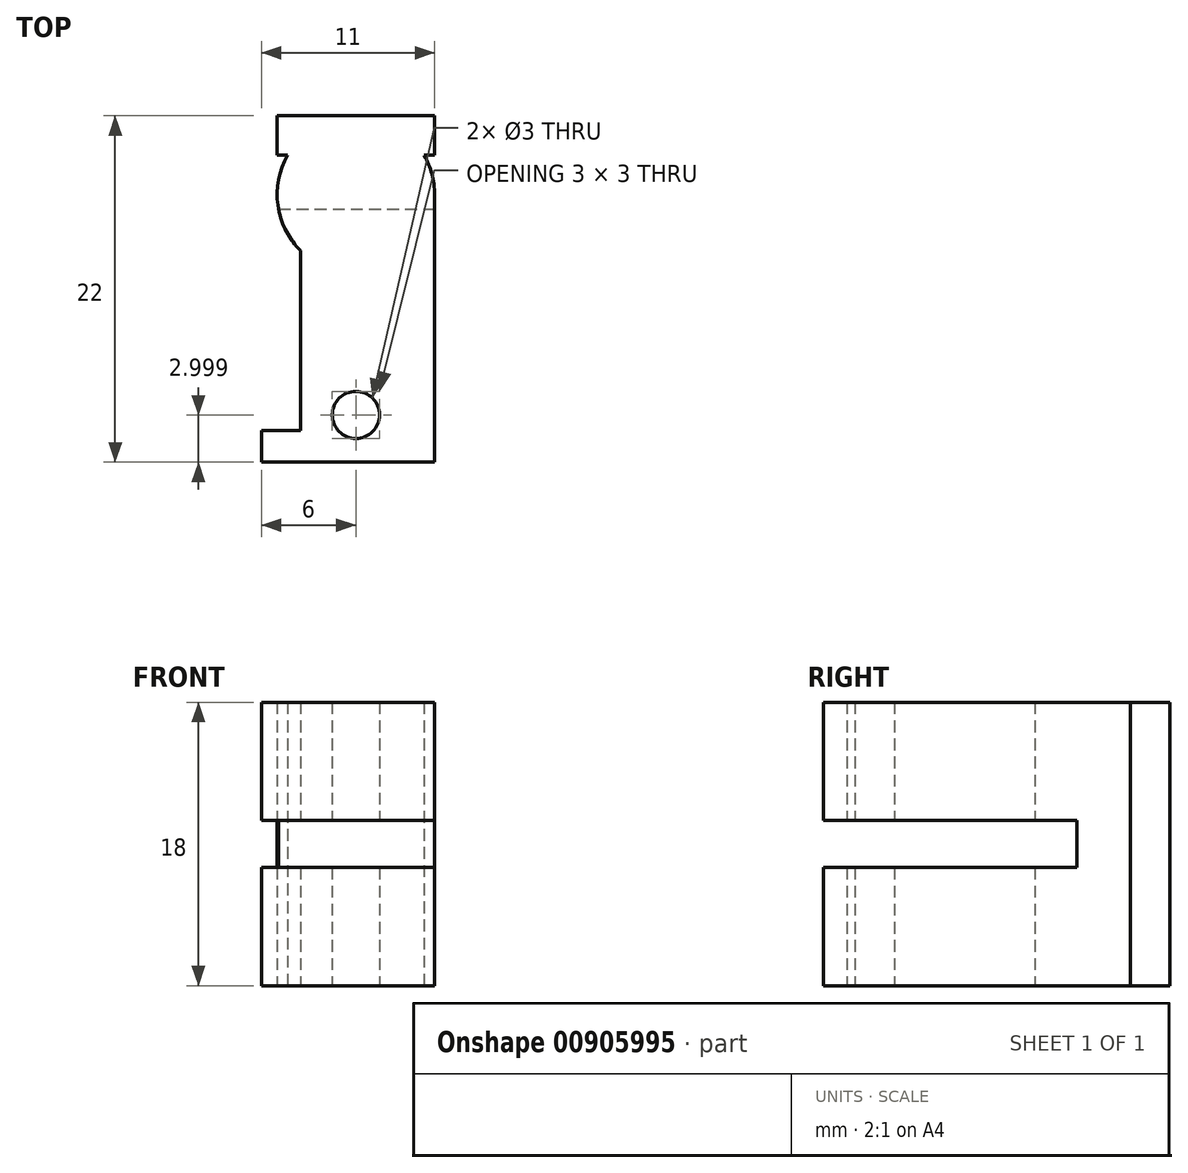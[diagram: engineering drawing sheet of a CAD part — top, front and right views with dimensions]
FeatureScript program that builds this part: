
annotation { "Feature Type Name" : "Feature", "Feature Type Description" : "" }
export const myFeature = defineFeature(function(context is Context, id is Id, definition is map)
    precondition{}
    {
        {
            var Q0;
            Q0=qCreatedBy(makeId("Top.planeOp"),FACE);
            var sketch = newSketch(context, id + "F0", { "sketchPlane" : qUnion([Q0])});
            skLineSegment(sketch, "E0.bottom", {"start": v(5, -1.25) * mm, "end": v(4.33, -1.25) * mm});
            skLineSegment(sketch, "E0.top", {"start": v(5, 1.25) * mm, "end": v(-5, 1.25) * mm});
            skLineSegment(sketch, "E0.left", {"start": v(5, -1.25) * mm, "end": v(5, 1.25) * mm});
            skLineSegment(sketch, "E0.right", {"start": v(-5, -1.25) * mm, "end": v(-5, 1.25) * mm});
            skPoint(sketch, "E0.middle", {"position": v(0, 0) * mm});
            skArc(sketch, "E1", {"start": v(5, -3.75) * mm, "mid": v(4.83, -2.46) * mm, "end": v(4.33, -1.25) * mm});
            skLineSegment(sketch, "E2.left", {"start": v(-3.5, -7.32) * mm, "end": v(-3.5, -18.75) * mm});
            skLineSegment(sketch, "E2.right", {"start": v(5, -3.75) * mm, "end": v(5, -18.75) * mm});
            skLineSegment(sketch, "E3.bottom", {"start": v(-3.5, -18.75) * mm, "end": v(-6, -18.75) * mm});
            skLineSegment(sketch, "E3.top", {"start": v(5, -20.75) * mm, "end": v(-6, -20.75) * mm});
            skLineSegment(sketch, "E3.left", {"start": v(5, -18.75) * mm, "end": v(5, -20.75) * mm});
            skLineSegment(sketch, "E3.right", {"start": v(-6, -18.75) * mm, "end": v(-6, -20.75) * mm});
            skCircle(sketch, "E4", {"center": v(0, -17.75) * mm, "radius": 1.5 * mm});
            skArc(sketch, "E5.trimOffspring", {"start": v(-4.33, -1.25) * mm, "mid": v(-4.95, -4.43) * mm, "end": v(-3.5, -7.32) * mm});
            skLineSegment(sketch, "E6.trimOffspring", {"start": v(-4.33, -1.25) * mm, "end": v(-5, -1.25) * mm});
            skSolve(sketch);
        }
        {
            var Q0;
            Q0=makeQuery(id+"F0.imprint","IMPRINT",FACE,{"disambiguationData":[TD([[makeQuery(id+"F0.imprint","IMPRINT",EDGE,{"derivedFrom":sQuery(id+"F0.wireOp",EDGE,"E0.bottom")}),-1.0]])]});
            extrude(context, id + "F1", {"entities" : qUnion([Q0]), "depth" : 18 * mm, "offsetDistance" : 25.4 * mm});
        }
        {
            var Q0;
            Q0=makeQuery(id+"F1.opExtrude","SWEPT_FACE",FACE,{"disambiguationData":[OSD([sQuery(id+"F0.wireOp",EDGE,"E2.right"),sQuery(id+"F0.wireOp",EDGE,"E3.left")])]});
            var sketch = newSketch(context, id + "F2", { "sketchPlane" : qUnion([Q0])});
            skLineSegment(sketch, "E7.bottom", {"start": v(-20.75, 7.5) * mm, "end": v(-4.66, 7.5) * mm});
            skLineSegment(sketch, "E7.top", {"start": v(-20.75, 10.5) * mm, "end": v(-4.66, 10.5) * mm});
            skLineSegment(sketch, "E7.left", {"start": v(-20.75, 7.5) * mm, "end": v(-20.75, 10.5) * mm});
            skLineSegment(sketch, "E7.right", {"start": v(-4.66, 7.5) * mm, "end": v(-4.66, 10.5) * mm});
            skPoint(sketch, "E7.middle", {"position": v(-12.7, 9) * mm});
            skPoint(sketch, "E7.middle.positionSnap0", {"position": v(-20.75, 9) * mm});
            skPoint(sketch, "E7.centerSnap0", {"position": v(-20.75, 9) * mm});
            skSolve(sketch);
        }
        {
            var Q0;
            Q0=makeQuery(id+"F2.imprint","IMPRINT",FACE,{"disambiguationData":[TD([[makeQuery(id+"F2.imprint","IMPRINT",EDGE,{"derivedFrom":sQuery(id+"F2.wireOp",EDGE,"E7.bottom")}),1.0]])]});
            extrude(context, id + "F3", {"entities" : qUnion([Q0]), "operationType" : NewBodyOperationType.REMOVE, "oppositeDirection" : true, "depth" : 11 * mm, "offsetDistance" : 25.4 * mm});
        }
    });
